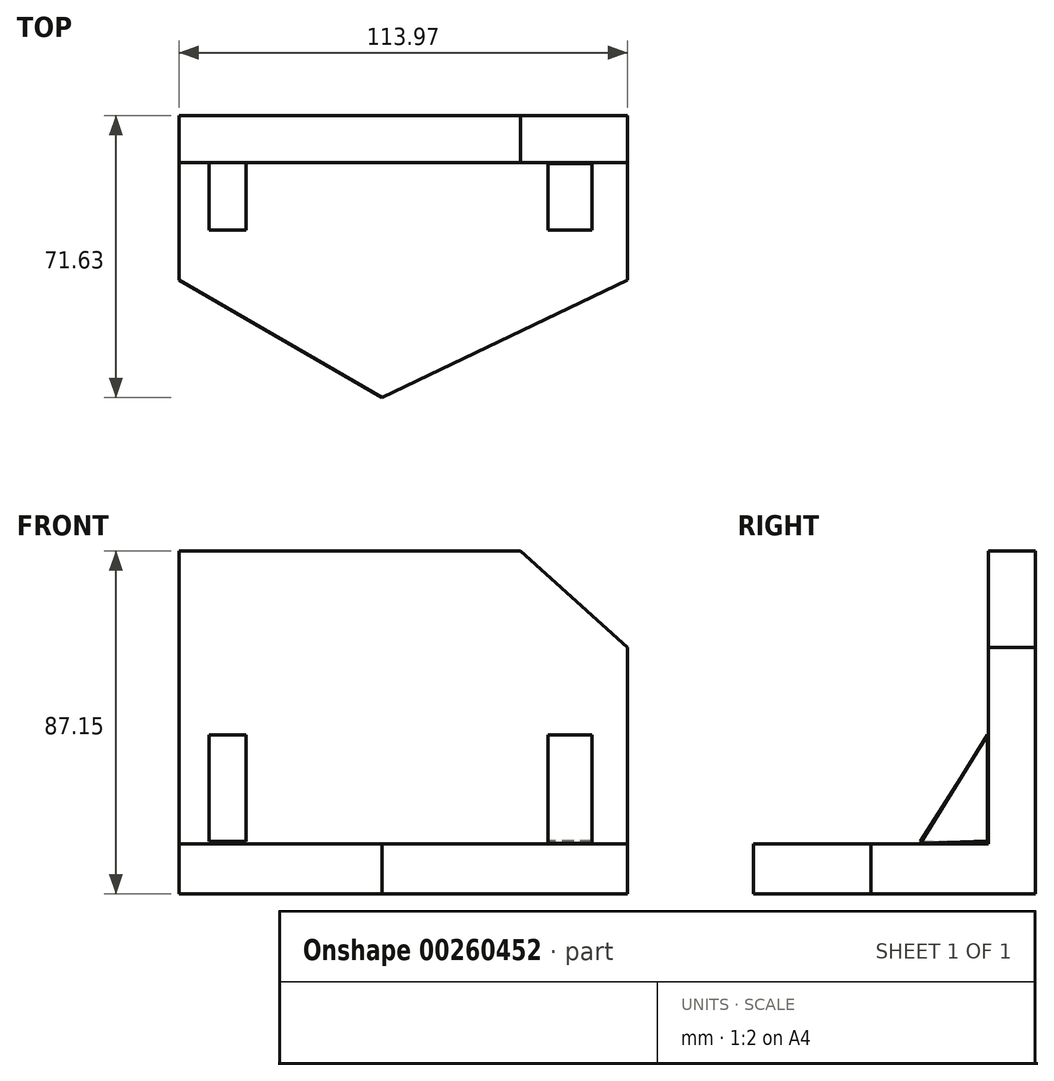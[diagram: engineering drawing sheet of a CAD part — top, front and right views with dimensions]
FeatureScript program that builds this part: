
annotation { "Feature Type Name" : "Feature", "Feature Type Description" : "" }
export const myFeature = defineFeature(function(context is Context, id is Id, definition is map)
    precondition{}
    {
        {
            var Q0;
            Q0=qCreatedBy(makeId("Front.planeOp"),FACE);
            var sketch = newSketch(context, id + "F0", { "sketchPlane" : qUnion([Q0])});
            skLineSegment(sketch, "E0.bottom", {"start": v(-51.6, 38.33) * mm, "end": v(62.38, 38.33) * mm});
            skLineSegment(sketch, "E0.top", {"start": v(-51.6, -48.82) * mm, "end": v(62.38, -48.82) * mm});
            skLineSegment(sketch, "E0.left", {"start": v(-51.6, 38.33) * mm, "end": v(-51.6, -48.82) * mm});
            skLineSegment(sketch, "E0.right", {"start": v(62.38, 38.33) * mm, "end": v(62.38, -48.82) * mm});
            skSolve(sketch);
        }
        {
            var Q0;
            Q0 = qSketchRegion(id + "F0", true);
            extrude(context, id + "F1", {"entities" : qUnion([Q0]), "depth" : 71.63 * mm});
        }
        {
            var Q0;
            Q0=makeQuery(id+"F1.opExtrude","CAP_FACE",FACE,{"disambiguationData":[OSD([sQuery(id+"F0.wireOp",EDGE,"E0.bottom"),sQuery(id+"F0.wireOp",EDGE,"E0.top"),sQuery(id+"F0.wireOp",EDGE,"E0.left"),sQuery(id+"F0.wireOp",EDGE,"E0.right")])],"isStart":false});
            var sketch = newSketch(context, id + "F2", { "sketchPlane" : qUnion([Q0])});
            skLineSegment(sketch, "E1", {"start": v(-51.6, -36.06) * mm, "end": v(62.38, -36.06) * mm});
            skSolve(sketch);
        }
        {
            var Q0;
            {var subQ0=sQuery(id+"F2.wireOp",EDGE,"E1");Q0=makeQuery(id+"F2.imprint","IMPRINT",FACE,{"disambiguationData":[TD([[makeQuery(id+"F2.imprint","IMPRINT",EDGE,{"derivedFrom":subQ0}),1.0]])]});}
            extrude(context, id + "F3", {"entities" : qUnion([Q0]), "operationType" : NewBodyOperationType.REMOVE, "oppositeDirection" : true, "depth" : 59.69 * mm});
        }
        {
            var Q0;
            Q0=makeQuery(id+"F3.boolean.opBoolean","COPY",FACE,{"derivedFrom":makeQuery(id+"F3.opExtrude","CAP_FACE",FACE,{"disambiguationData":[OSD([sQuery(id+"F0.wireOp",EDGE,"E0.bottom"),sQuery(id+"F0.wireOp",EDGE,"E0.left"),sQuery(id+"F0.wireOp",EDGE,"E0.right"),sQuery(id+"F2.wireOp",EDGE,"E1")])],"isStart":false})});
            var sketch = newSketch(context, id + "F4", { "sketchPlane" : qUnion([Q0])});
            skLineSegment(sketch, "E2", {"start": v(-23, 38.33) * mm, "end": v(-51.6, 15.6) * mm});
            skLineSegment(sketch, "E3", {"start": v(-51.6, 15.6) * mm, "end": v(-23, 38.33) * mm});
            skLineSegment(sketch, "E4", {"start": v(35.27, 38.33) * mm, "end": v(62.38, 13.85) * mm});
            skSolve(sketch);
        }
        {
            var Q0;
            {var subQ0=sQuery(id+"F4.wireOp",EDGE,"E3");Q0=makeQuery(id+"F4.imprint","IMPRINT",FACE,{"disambiguationData":[TD([[makeQuery(id+"F4.imprint","IMPRINT",EDGE,{"derivedFrom":subQ0}),1.0]])]});}
            var Q1;
            {var subQ0=sQuery(id+"F4.wireOp",EDGE,"E4");Q1=makeQuery(id+"F4.imprint","IMPRINT",FACE,{"disambiguationData":[TD([[makeQuery(id+"F4.imprint","IMPRINT",EDGE,{"derivedFrom":subQ0}),1.0]])]});}
            extrude(context, id + "F5", {"entities" : qUnion([Q0, Q1]), "operationType" : NewBodyOperationType.REMOVE, "oppositeDirection" : true, "depth" : 25.4 * mm});
        }
        {
            var Q0;
            Q0=makeQuery(id+"F3.boolean.opBoolean","COPY",FACE,{"derivedFrom":makeQuery(id+"F3.opExtrude","SWEPT_FACE",FACE,{"disambiguationData":[OSD([sQuery(id+"F2.wireOp",EDGE,"E1")])]})});
            var sketch = newSketch(context, id + "F6", { "sketchPlane" : qUnion([Q0])});
            skLineSegment(sketch, "E5", {"start": v(-51.6, -41.78) * mm, "end": v(0, -71.63) * mm});
            skLineSegment(sketch, "E6", {"start": v(0, -71.63) * mm, "end": v(62.38, -41.78) * mm});
            skSolve(sketch);
        }
        {
            var Q0;
            {var subQ0=sQuery(id+"F6.wireOp",EDGE,"E5");Q0=makeQuery(id+"F6.imprint","IMPRINT",FACE,{"disambiguationData":[TD([[makeQuery(id+"F6.imprint","IMPRINT",EDGE,{"derivedFrom":subQ0}),-1.0]])]});}
            var Q1;
            {var subQ0=sQuery(id+"F6.wireOp",EDGE,"E6");Q1=makeQuery(id+"F6.imprint","IMPRINT",FACE,{"disambiguationData":[TD([[makeQuery(id+"F6.imprint","IMPRINT",EDGE,{"derivedFrom":subQ0}),-1.0]])]});}
            extrude(context, id + "F7", {"entities" : qUnion([Q0, Q1]), "operationType" : NewBodyOperationType.REMOVE, "oppositeDirection" : true, "depth" : 25.4 * mm});
        }
        {
            var Q0;
            Q0=qCreatedBy(makeId("Right.planeOp"),FACE);
            var sketch = newSketch(context, id + "F8", { "sketchPlane" : qUnion([Q0])});
            skLineSegment(sketch, "E7", {"start": v(-12.15, -35.32) * mm, "end": v(-12.15, -8.36) * mm});
            skLineSegment(sketch, "E8", {"start": v(-12.15, -8.36) * mm, "end": v(-29.15, -35.92) * mm});
            skLineSegment(sketch, "E9", {"start": v(-29.15, -35.92) * mm, "end": v(-12.15, -35.32) * mm});
            skSolve(sketch);
        }
        {
            var Q0;
            Q0 = qSketchRegion(id + "F8", true);
            extrude(context, id + "F9", {"entities" : qUnion([Q0]), "depth" : 53.34 * mm});
        }
        {
            var Q0;
            Q0=makeQuery(id+"F9.opExtrude","CAP_FACE",FACE,{"disambiguationData":[OSD([sQuery(id+"F8.wireOp",EDGE,"E7"),sQuery(id+"F8.wireOp",EDGE,"E8"),sQuery(id+"F8.wireOp",EDGE,"E9")])],"isStart":true});
            extrude(context, id + "F10", {"entities" : qUnion([Q0]), "operationType" : NewBodyOperationType.REMOVE, "oppositeDirection" : true, "depth" : 42.16 * mm});
        }
        {
            var Q0;
            Q0=qCreatedBy(makeId("Right.planeOp"),FACE);
            var sketch = newSketch(context, id + "F11", { "sketchPlane" : qUnion([Q0])});
            skLineSegment(sketch, "E10", {"start": v(-29.15, -35.41) * mm, "end": v(-11.66, -35.41) * mm});
            skLineSegment(sketch, "E11", {"start": v(-11.66, -35.41) * mm, "end": v(-11.66, -8.02) * mm});
            skLineSegment(sketch, "E12", {"start": v(-11.66, -8.02) * mm, "end": v(-29.15, -35.41) * mm});
            skSolve(sketch);
        }
        {
            var Q0;
            Q0=makeQuery(id+"F11.imprint","IMPRINT",FACE,{"disambiguationData":[TD([[makeQuery(id+"F11.imprint","IMPRINT",EDGE,{"derivedFrom":sQuery(id+"F11.wireOp",EDGE,"E10")}),1.0]])]});
            extrude(context, id + "F12", {"entities" : qUnion([Q0]), "operationType" : NewBodyOperationType.ADD, "oppositeDirection" : true, "depth" : 43.94 * mm});
        }
        {
            var Q0;
            Q0=makeQuery(id+"F12.opExtrude","CAP_FACE",FACE,{"disambiguationData":[OSD([sQuery(id+"F11.wireOp",EDGE,"E10"),sQuery(id+"F11.wireOp",EDGE,"E11"),sQuery(id+"F11.wireOp",EDGE,"E12")])],"isStart":true});
            extrude(context, id + "F13", {"entities" : qUnion([Q0]), "operationType" : NewBodyOperationType.REMOVE, "oppositeDirection" : true, "depth" : 34.54 * mm});
        }
    });
